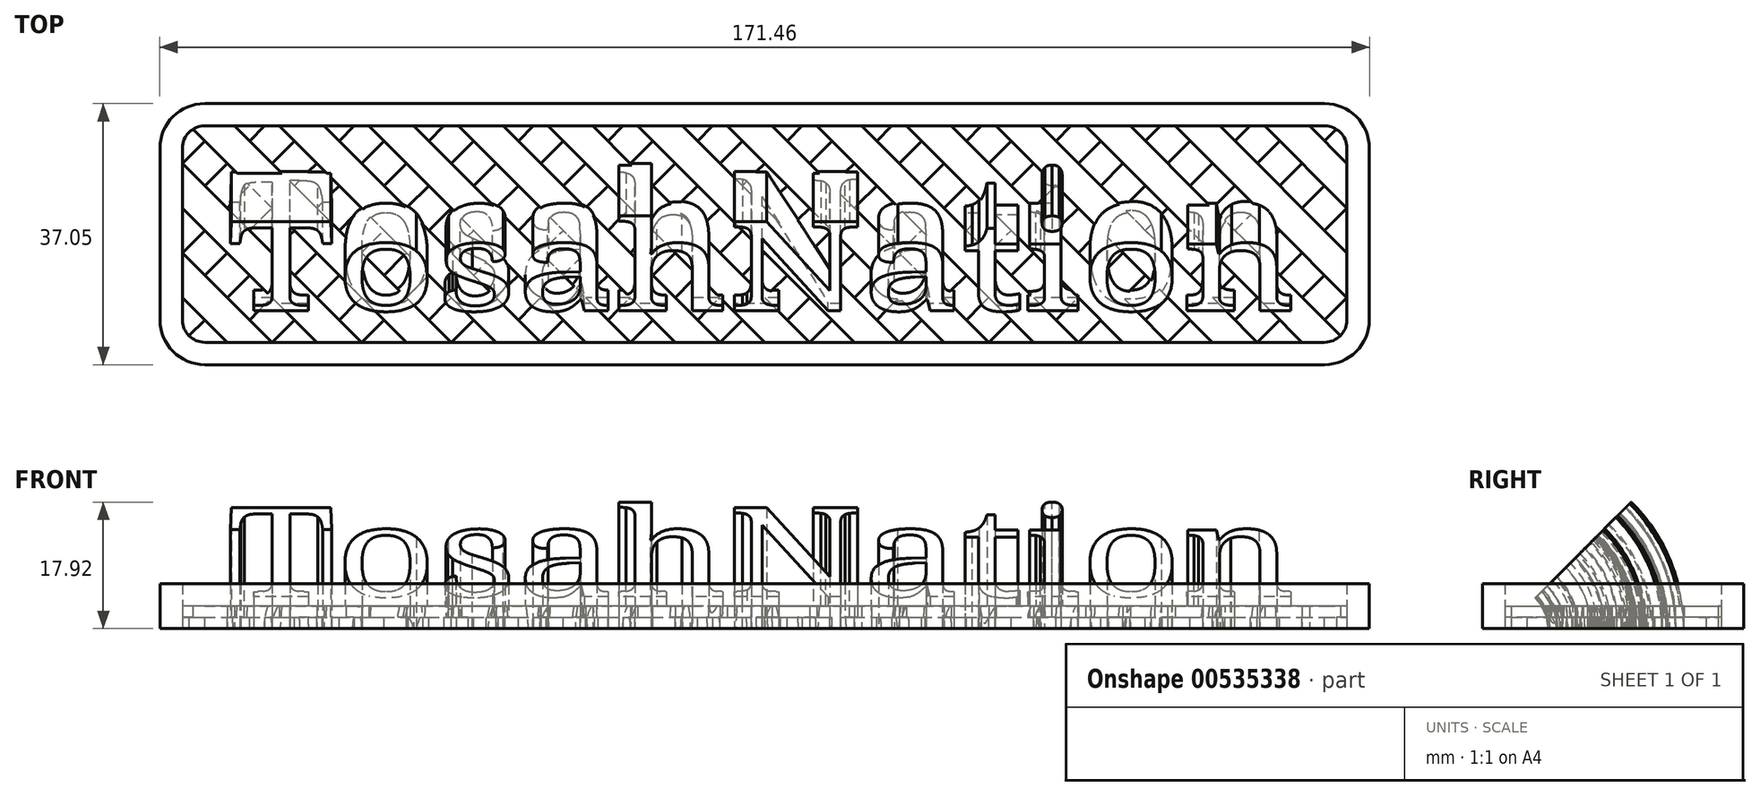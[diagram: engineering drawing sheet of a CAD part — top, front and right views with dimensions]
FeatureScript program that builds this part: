
annotation { "Feature Type Name" : "Feature", "Feature Type Description" : "" }
export const myFeature = defineFeature(function(context is Context, id is Id, definition is map)
    precondition{}
    {
        {
            var Q0;
            Q0=qCreatedBy(makeId("Top.planeOp"),FACE);
            var sketch = newSketch(context, id + "F0", { "sketchPlane" : qUnion([Q0])});
            skText(sketch, "E0", { "text": "TosahNation", "fontName": "NotoSerif-Regular.ttf"});
            skLineSegment(sketch, "E1", {"start": v(-76.2, 0) * mm, "end": v(-76.2, -6.35) * mm, "construction": true});
            skLineSegment(sketch, "E2", {"start": v(-76.2, -6.35) * mm, "end": v(-58.68, -6.35) * mm, "construction": true});
            const initialGuessF0  = {"E0": [-0.0762, 0, 1, 0, 0.018]};
            skSetInitialGuess(sketch, initialGuessF0);
            skSolve(sketch);
        }
        {
            var Q0;
            Q0=qCreatedBy(makeId("Top.planeOp"),FACE);
            var sketch = newSketch(context, id + "F1", { "sketchPlane" : qUnion([Q0])});
            skLineSegment(sketch, "E3", {"start": v(-82.55, -3.18) * mm, "end": v(-82.55, 21.17) * mm});
            skLineSegment(sketch, "E4", {"start": v(-79.37, 24.35) * mm, "end": v(79.37, 24.35) * mm});
            skLineSegment(sketch, "E5", {"start": v(82.55, 21.17) * mm, "end": v(82.55, -3.17) * mm});
            skLineSegment(sketch, "E6", {"start": v(79.37, -6.35) * mm, "end": v(-79.37, -6.35) * mm});
            skLineSegment(sketch, "E7", {"start": v(-81.62, -5.42) * mm, "end": v(-51.85, 24.35) * mm});
            skLineSegment(sketch, "E8.1.0.0", {"start": v(-76.2, -6.35) * mm, "end": v(-45.5, 24.35) * mm});
            skLineSegment(sketch, "E8.2.0.0", {"start": v(-69.85, -6.35) * mm, "end": v(-39.15, 24.35) * mm});
            skLineSegment(sketch, "E8.3.0.0", {"start": v(-63.5, -6.35) * mm, "end": v(-32.8, 24.35) * mm});
            skLineSegment(sketch, "E8.4.0.0", {"start": v(-57.15, -6.35) * mm, "end": v(-26.45, 24.35) * mm});
            skLineSegment(sketch, "E8.5.0.0", {"start": v(-50.8, -6.35) * mm, "end": v(-20.1, 24.35) * mm});
            skLineSegment(sketch, "E8.6.0.0", {"start": v(-44.45, -6.35) * mm, "end": v(-13.75, 24.35) * mm});
            skLineSegment(sketch, "E8.7.0.0", {"start": v(-38.1, -6.35) * mm, "end": v(-7.4, 24.35) * mm});
            skLineSegment(sketch, "E8.8.0.0", {"start": v(-31.75, -6.35) * mm, "end": v(-1.05, 24.35) * mm});
            skLineSegment(sketch, "E8.9.0.0", {"start": v(-25.4, -6.35) * mm, "end": v(5.3, 24.35) * mm});
            skLineSegment(sketch, "E8.10.0.0", {"start": v(-19.05, -6.35) * mm, "end": v(11.65, 24.35) * mm});
            skLineSegment(sketch, "E8.11.0.0", {"start": v(-12.7, -6.35) * mm, "end": v(18, 24.35) * mm});
            skLineSegment(sketch, "E8.12.0.0", {"start": v(-6.35, -6.35) * mm, "end": v(24.35, 24.35) * mm});
            skLineSegment(sketch, "E8.13.0.0", {"start": v(0, -6.35) * mm, "end": v(30.7, 24.35) * mm});
            skLineSegment(sketch, "E8.14.0.0", {"start": v(6.35, -6.35) * mm, "end": v(37.05, 24.35) * mm});
            skLineSegment(sketch, "E8.15.0.0", {"start": v(12.7, -6.35) * mm, "end": v(43.4, 24.35) * mm});
            skLineSegment(sketch, "E8.16.0.0", {"start": v(19.05, -6.35) * mm, "end": v(49.75, 24.35) * mm});
            skLineSegment(sketch, "E8.17.0.0", {"start": v(25.4, -6.35) * mm, "end": v(56.1, 24.35) * mm});
            skLineSegment(sketch, "E8.18.0.0", {"start": v(31.75, -6.35) * mm, "end": v(62.45, 24.35) * mm});
            skLineSegment(sketch, "E8.19.0.0", {"start": v(38.1, -6.35) * mm, "end": v(68.8, 24.35) * mm});
            skLineSegment(sketch, "E8.20.0.0", {"start": v(44.45, -6.35) * mm, "end": v(75.15, 24.35) * mm});
            skLineSegment(sketch, "E8.21.0.0", {"start": v(50.8, -6.35) * mm, "end": v(81.03, 23.88) * mm});
            skLineSegment(sketch, "E8.22.0.0", {"start": v(57.15, -6.35) * mm, "end": v(82.55, 19.05) * mm});
            skLineSegment(sketch, "E8.23.0.0", {"start": v(63.5, -6.35) * mm, "end": v(82.55, 12.7) * mm});
            skLineSegment(sketch, "E8.24.0.0", {"start": v(69.85, -6.35) * mm, "end": v(82.55, 6.35) * mm});
            skLineSegment(sketch, "E8.25.0.0", {"start": v(76.2, -6.35) * mm, "end": v(82.55, 0) * mm});
            skLineSegment(sketch, "E8.direction1", {"start": v(-82.55, -6.35) * mm, "end": v(-76.2, -6.35) * mm, "construction": true});
            skLineSegment(sketch, "E9.1.0.0", {"start": v(-82.55, 0) * mm, "end": v(-58.2, 24.35) * mm});
            skLineSegment(sketch, "E9.2.0.0", {"start": v(-82.55, 6.35) * mm, "end": v(-64.55, 24.35) * mm});
            skLineSegment(sketch, "E9.3.0.0", {"start": v(-82.55, 12.7) * mm, "end": v(-70.9, 24.35) * mm});
            skLineSegment(sketch, "E9.4.0.0", {"start": v(-82.55, 19.05) * mm, "end": v(-77.25, 24.35) * mm});
            skLineSegment(sketch, "E9.direction1", {"start": v(-82.55, -6.35) * mm, "end": v(-88.9, -6.35) * mm, "construction": true});
            skPoint(sketch, "E10.orphan", {"position": v(-107.95, -6.35) * mm});
            skPoint(sketch, "E11.orphan", {"position": v(-101.6, -6.35) * mm});
            skPoint(sketch, "E12.orphan", {"position": v(-95.25, -6.35) * mm});
            skPoint(sketch, "E13.orphan", {"position": v(-49.82, 51.78) * mm});
            skPoint(sketch, "E14.orphan", {"position": v(-43.47, 51.78) * mm});
            skPoint(sketch, "E15.orphan", {"position": v(-37.12, 51.78) * mm});
            skPoint(sketch, "E16.orphan", {"position": v(-30.77, 51.78) * mm});
            skPoint(sketch, "E17.orphan", {"position": v(-24.42, 51.78) * mm});
            skPoint(sketch, "E18.orphan", {"position": v(-18.07, 51.78) * mm});
            skPoint(sketch, "E19.orphan", {"position": v(-11.72, 51.78) * mm});
            skPoint(sketch, "E20.orphan", {"position": v(-5.37, 51.78) * mm});
            skPoint(sketch, "E21.orphan", {"position": v(0.98, 51.78) * mm});
            skPoint(sketch, "E22.orphan", {"position": v(7.33, 51.78) * mm});
            skPoint(sketch, "E23.orphan", {"position": v(13.68, 51.78) * mm});
            skPoint(sketch, "E24.orphan", {"position": v(20.03, 51.78) * mm});
            skPoint(sketch, "E25.orphan", {"position": v(58.13, 51.78) * mm});
            skPoint(sketch, "E26.orphan", {"position": v(64.48, 51.78) * mm});
            skPoint(sketch, "E27.orphan", {"position": v(70.83, 51.78) * mm});
            skPoint(sketch, "E28.orphan", {"position": v(77.18, 51.78) * mm});
            skPoint(sketch, "E29.orphan", {"position": v(83.53, 51.78) * mm});
            skPoint(sketch, "E30.orphan", {"position": v(89.88, 51.78) * mm});
            skPoint(sketch, "E31.orphan", {"position": v(96.23, 51.78) * mm});
            skPoint(sketch, "E32.orphan", {"position": v(102.58, 51.78) * mm});
            skPoint(sketch, "E33.orphan", {"position": v(108.93, 51.78) * mm});
            skPoint(sketch, "E34.orphan", {"position": v(115.28, 51.78) * mm});
            skPoint(sketch, "E35.orphan", {"position": v(121.63, 51.78) * mm});
            skPoint(sketch, "E36.orphan", {"position": v(127.98, 51.78) * mm});
            skPoint(sketch, "E37.orphan", {"position": v(134.33, 51.78) * mm});
            skPoint(sketch, "E38.visualSharp", {"position": v(-82.55, 24.35) * mm});
            skArc(sketch, "E38.filletArc", {"start": v(-79.37, 24.35) * mm, "mid": v(-81.62, 23.42) * mm, "end": v(-82.55, 21.17) * mm});
            skPoint(sketch, "E39.visualSharp", {"position": v(-82.55, -6.35) * mm});
            skArc(sketch, "E39.filletArc", {"start": v(-82.55, -3.18) * mm, "mid": v(-81.62, -5.42) * mm, "end": v(-79.37, -6.35) * mm});
            skPoint(sketch, "E40.visualSharp", {"position": v(82.55, 24.35) * mm});
            skArc(sketch, "E40.filletArc", {"start": v(82.55, 21.17) * mm, "mid": v(81.62, 23.42) * mm, "end": v(79.37, 24.35) * mm});
            skPoint(sketch, "E41.visualSharp", {"position": v(82.55, -6.35) * mm});
            skArc(sketch, "E41.filletArc", {"start": v(79.37, -6.35) * mm, "mid": v(81.62, -5.42) * mm, "end": v(82.55, -3.17) * mm});
            skArc(sketch, "E42.0", {"start": v(-85.72, -3.18) * mm, "mid": v(-83.87, -7.67) * mm, "end": v(-79.37, -9.53) * mm});
            skLineSegment(sketch, "E42.1", {"start": v(79.37, -9.52) * mm, "end": v(-79.37, -9.53) * mm});
            skLineSegment(sketch, "E42.2", {"start": v(-85.72, -3.18) * mm, "end": v(-85.72, 21.17) * mm});
            skArc(sketch, "E42.3", {"start": v(79.37, -9.53) * mm, "mid": v(83.87, -7.67) * mm, "end": v(85.72, -3.17) * mm});
            skArc(sketch, "E42.4", {"start": v(-79.37, 27.52) * mm, "mid": v(-83.87, 25.66) * mm, "end": v(-85.72, 21.17) * mm});
            skLineSegment(sketch, "E42.5", {"start": v(-79.37, 27.52) * mm, "end": v(79.37, 27.52) * mm});
            skArc(sketch, "E42.6", {"start": v(85.72, 21.17) * mm, "mid": v(83.87, 25.66) * mm, "end": v(79.37, 27.52) * mm});
            skLineSegment(sketch, "E42.7", {"start": v(85.72, 21.17) * mm, "end": v(85.72, -3.17) * mm});
            skSolve(sketch);
        }
        {
            var Q0;
            {var subQ54=sQuery(id+"F1.wireOp",EDGE,"E38.filletArc");Q0=makeQuery(id+"F1.imprint","IMPRINT",FACE,{"disambiguationData":[TD([[makeQuery(id+"F1.imprint","IMPRINT",EDGE,{"derivedFrom":subQ54}),-1.0]])]});}
            extrude(context, id + "F2", {"entities" : qUnion([Q0]), "depth" : 6.35 * mm, "offsetDistance" : 25.4 * mm});
        }
        {
            var Q0;
            {var subQ0=sQuery(id+"F1.wireOp",EDGE,"E8.15.0.0");Q0=makeQuery(id+"F1.imprint","IMPRINT",FACE,{"disambiguationData":[TD([[makeQuery(id+"F1.imprint","IMPRINT",EDGE,{"derivedFrom":subQ0}),-1.0]])]});}
            var Q1;
            {var subQ0=sQuery(id+"F1.wireOp",EDGE,"E8.17.0.0");Q1=makeQuery(id+"F1.imprint","IMPRINT",FACE,{"disambiguationData":[TD([[makeQuery(id+"F1.imprint","IMPRINT",EDGE,{"derivedFrom":subQ0}),-1.0]])]});}
            var Q2;
            {var subQ0=sQuery(id+"F1.wireOp",EDGE,"E8.19.0.0");Q2=makeQuery(id+"F1.imprint","IMPRINT",FACE,{"disambiguationData":[TD([[makeQuery(id+"F1.imprint","IMPRINT",EDGE,{"derivedFrom":subQ0}),-1.0]])]});}
            var Q3;
            {var subQ1=sQuery(id+"F1.wireOp",EDGE,"E8.21.0.0");Q3=makeQuery(id+"F1.imprint","IMPRINT",FACE,{"disambiguationData":[TD([[makeQuery(id+"F1.imprint","IMPRINT",EDGE,{"derivedFrom":subQ1}),-1.0]])]});}
            var Q4;
            {var subQ2=sQuery(id+"F1.wireOp",EDGE,"E8.25.0.0");Q4=makeQuery(id+"F1.imprint","IMPRINT",FACE,{"disambiguationData":[TD([[makeQuery(id+"F1.imprint","IMPRINT",EDGE,{"derivedFrom":subQ2}),-1.0]])]});}
            var Q5;
            {var subQ0=sQuery(id+"F1.wireOp",EDGE,"E8.23.0.0");Q5=makeQuery(id+"F1.imprint","IMPRINT",FACE,{"disambiguationData":[TD([[makeQuery(id+"F1.imprint","IMPRINT",EDGE,{"derivedFrom":subQ0}),-1.0]])]});}
            var Q6;
            {var subQ0=sQuery(id+"F1.wireOp",EDGE,"E8.13.0.0");Q6=makeQuery(id+"F1.imprint","IMPRINT",FACE,{"disambiguationData":[TD([[makeQuery(id+"F1.imprint","IMPRINT",EDGE,{"derivedFrom":subQ0}),-1.0]])]});}
            var Q7;
            {var subQ0=sQuery(id+"F1.wireOp",EDGE,"E8.11.0.0");Q7=makeQuery(id+"F1.imprint","IMPRINT",FACE,{"disambiguationData":[TD([[makeQuery(id+"F1.imprint","IMPRINT",EDGE,{"derivedFrom":subQ0}),-1.0]])]});}
            var Q8;
            {var subQ0=sQuery(id+"F1.wireOp",EDGE,"E8.9.0.0");Q8=makeQuery(id+"F1.imprint","IMPRINT",FACE,{"disambiguationData":[TD([[makeQuery(id+"F1.imprint","IMPRINT",EDGE,{"derivedFrom":subQ0}),-1.0]])]});}
            var Q9;
            {var subQ0=sQuery(id+"F1.wireOp",EDGE,"E8.7.0.0");Q9=makeQuery(id+"F1.imprint","IMPRINT",FACE,{"disambiguationData":[TD([[makeQuery(id+"F1.imprint","IMPRINT",EDGE,{"derivedFrom":subQ0}),-1.0]])]});}
            var Q10;
            {var subQ0=sQuery(id+"F1.wireOp",EDGE,"E8.5.0.0");Q10=makeQuery(id+"F1.imprint","IMPRINT",FACE,{"disambiguationData":[TD([[makeQuery(id+"F1.imprint","IMPRINT",EDGE,{"derivedFrom":subQ0}),-1.0]])]});}
            var Q11;
            {var subQ0=sQuery(id+"F1.wireOp",EDGE,"E8.3.0.0");Q11=makeQuery(id+"F1.imprint","IMPRINT",FACE,{"disambiguationData":[TD([[makeQuery(id+"F1.imprint","IMPRINT",EDGE,{"derivedFrom":subQ0}),-1.0]])]});}
            var Q12;
            {var subQ0=sQuery(id+"F1.wireOp",EDGE,"E8.1.0.0");Q12=makeQuery(id+"F1.imprint","IMPRINT",FACE,{"disambiguationData":[TD([[makeQuery(id+"F1.imprint","IMPRINT",EDGE,{"derivedFrom":subQ0}),-1.0]])]});}
            var Q13;
            {var subQ4=sQuery(id+"F1.wireOp",EDGE,"E7");Q13=makeQuery(id+"F1.imprint","IMPRINT",FACE,{"disambiguationData":[TD([[makeQuery(id+"F1.imprint","IMPRINT",EDGE,{"derivedFrom":subQ4}),1.0]])]});}
            var Q14;
            {var subQ0=sQuery(id+"F1.wireOp",EDGE,"E9.2.0.0");Q14=makeQuery(id+"F1.imprint","IMPRINT",FACE,{"disambiguationData":[TD([[makeQuery(id+"F1.imprint","IMPRINT",EDGE,{"derivedFrom":subQ0}),1.0]])]});}
            var Q15;
            {var subQ2=sQuery(id+"F1.wireOp",EDGE,"E9.4.0.0");Q15=makeQuery(id+"F1.imprint","IMPRINT",FACE,{"disambiguationData":[TD([[makeQuery(id+"F1.imprint","IMPRINT",EDGE,{"derivedFrom":subQ2}),1.0]])]});}
            extrude(context, id + "F3", {"entities" : qUnion([Q0, Q1, Q2, Q3, Q4, Q5, Q6, Q7, Q8, Q9, Q10, Q11, Q12, Q13, Q14, Q15]), "operationType" : NewBodyOperationType.ADD, "depth" : 1.59 * mm, "offsetDistance" : 25.4 * mm});
        }
        {
            var Q0;
            Q0=qCreatedBy(makeId("Top.planeOp"),FACE);
            var sketch = newSketch(context, id + "F4", { "sketchPlane" : qUnion([Q0])});
            skLineSegment(sketch, "E43", {"start": v(82.55, -6.35) * mm, "end": v(51.85, 24.35) * mm});
            skLineSegment(sketch, "E44.1.0.0", {"start": v(76.2, -6.35) * mm, "end": v(45.5, 24.35) * mm});
            skLineSegment(sketch, "E44.2.0.0", {"start": v(69.85, -6.35) * mm, "end": v(39.15, 24.35) * mm});
            skLineSegment(sketch, "E44.3.0.0", {"start": v(63.5, -6.35) * mm, "end": v(32.8, 24.35) * mm});
            skLineSegment(sketch, "E44.4.0.0", {"start": v(57.15, -6.35) * mm, "end": v(26.45, 24.35) * mm});
            skLineSegment(sketch, "E44.5.0.0", {"start": v(50.8, -6.35) * mm, "end": v(20.1, 24.35) * mm});
            skLineSegment(sketch, "E44.6.0.0", {"start": v(44.45, -6.35) * mm, "end": v(13.75, 24.35) * mm});
            skLineSegment(sketch, "E44.7.0.0", {"start": v(38.1, -6.35) * mm, "end": v(7.4, 24.35) * mm});
            skLineSegment(sketch, "E44.8.0.0", {"start": v(31.75, -6.35) * mm, "end": v(1.05, 24.35) * mm});
            skLineSegment(sketch, "E44.9.0.0", {"start": v(25.4, -6.35) * mm, "end": v(-5.3, 24.35) * mm});
            skLineSegment(sketch, "E44.10.0.0", {"start": v(19.05, -6.35) * mm, "end": v(-11.65, 24.35) * mm});
            skLineSegment(sketch, "E44.11.0.0", {"start": v(12.7, -6.35) * mm, "end": v(-18, 24.35) * mm});
            skLineSegment(sketch, "E44.12.0.0", {"start": v(6.35, -6.35) * mm, "end": v(-24.35, 24.35) * mm});
            skLineSegment(sketch, "E44.13.0.0", {"start": v(0, -6.35) * mm, "end": v(-30.7, 24.35) * mm});
            skLineSegment(sketch, "E44.14.0.0", {"start": v(-6.35, -6.35) * mm, "end": v(-37.05, 24.35) * mm});
            skLineSegment(sketch, "E44.15.0.0", {"start": v(-12.7, -6.35) * mm, "end": v(-43.4, 24.35) * mm});
            skLineSegment(sketch, "E44.16.0.0", {"start": v(-19.05, -6.35) * mm, "end": v(-49.75, 24.35) * mm});
            skLineSegment(sketch, "E44.17.0.0", {"start": v(-25.4, -6.35) * mm, "end": v(-56.1, 24.35) * mm});
            skLineSegment(sketch, "E44.18.0.0", {"start": v(-31.75, -6.35) * mm, "end": v(-62.45, 24.35) * mm});
            skLineSegment(sketch, "E44.19.0.0", {"start": v(-38.1, -6.35) * mm, "end": v(-68.8, 24.35) * mm});
            skLineSegment(sketch, "E44.20.0.0", {"start": v(-44.45, -6.35) * mm, "end": v(-75.15, 24.35) * mm});
            skLineSegment(sketch, "E44.21.0.0", {"start": v(-50.8, -6.35) * mm, "end": v(-81.5, 24.35) * mm});
            skLineSegment(sketch, "E44.22.0.0", {"start": v(-57.15, -6.35) * mm, "end": v(-82.55, 19.05) * mm});
            skLineSegment(sketch, "E44.23.0.0", {"start": v(-63.5, -6.35) * mm, "end": v(-82.55, 12.7) * mm});
            skLineSegment(sketch, "E44.24.0.0", {"start": v(-69.85, -6.35) * mm, "end": v(-82.55, 6.35) * mm});
            skLineSegment(sketch, "E44.25.0.0", {"start": v(-76.2, -6.35) * mm, "end": v(-82.55, 0) * mm});
            skLineSegment(sketch, "E44.direction1", {"start": v(82.55, -6.35) * mm, "end": v(76.2, -6.35) * mm, "construction": true});
            skLineSegment(sketch, "E45.bottom", {"start": v(-82.55, 24.35) * mm, "end": v(82.55, 24.35) * mm});
            skLineSegment(sketch, "E45.top", {"start": v(-82.55, -6.35) * mm, "end": v(82.55, -6.35) * mm});
            skLineSegment(sketch, "E45.left", {"start": v(-82.55, 24.35) * mm, "end": v(-82.55, -6.35) * mm});
            skLineSegment(sketch, "E45.right", {"start": v(82.55, 24.35) * mm, "end": v(82.55, -6.35) * mm});
            skLineSegment(sketch, "E46.1.0.0", {"start": v(82.55, 0) * mm, "end": v(58.2, 24.35) * mm});
            skLineSegment(sketch, "E46.2.0.0", {"start": v(82.55, 6.35) * mm, "end": v(64.55, 24.35) * mm});
            skLineSegment(sketch, "E46.3.0.0", {"start": v(82.55, 12.7) * mm, "end": v(70.9, 24.35) * mm});
            skLineSegment(sketch, "E46.4.0.0", {"start": v(82.55, 19.05) * mm, "end": v(77.25, 24.35) * mm});
            skLineSegment(sketch, "E46.direction1", {"start": v(82.55, -6.35) * mm, "end": v(88.9, -6.35) * mm, "construction": true});
            skPoint(sketch, "E47.orphan", {"position": v(107.95, -6.35) * mm});
            skPoint(sketch, "E48.orphan", {"position": v(101.6, -6.35) * mm});
            skPoint(sketch, "E49.orphan", {"position": v(95.25, -6.35) * mm});
            skPoint(sketch, "E50.orphan", {"position": v(67.41, 34.19) * mm});
            skPoint(sketch, "E51.orphan", {"position": v(61.06, 34.19) * mm});
            skPoint(sketch, "E52.orphan", {"position": v(54.71, 34.19) * mm});
            skPoint(sketch, "E53.orphan", {"position": v(48.36, 34.19) * mm});
            skPoint(sketch, "E54.orphan", {"position": v(42.01, 34.19) * mm});
            skPoint(sketch, "E55.orphan", {"position": v(35.66, 34.19) * mm});
            skPoint(sketch, "E56.orphan", {"position": v(29.31, 34.19) * mm});
            skPoint(sketch, "E57.orphan", {"position": v(22.96, 34.19) * mm});
            skPoint(sketch, "E58.orphan", {"position": v(16.61, 34.19) * mm});
            skPoint(sketch, "E59.orphan", {"position": v(10.26, 34.19) * mm});
            skPoint(sketch, "E60.orphan", {"position": v(3.91, 34.19) * mm});
            skPoint(sketch, "E61.orphan", {"position": v(-2.44, 34.19) * mm});
            skPoint(sketch, "E62.orphan", {"position": v(-8.79, 34.19) * mm});
            skPoint(sketch, "E63.orphan", {"position": v(-15.14, 34.19) * mm});
            skPoint(sketch, "E64.orphan", {"position": v(-21.49, 34.19) * mm});
            skPoint(sketch, "E65.orphan", {"position": v(-27.84, 34.19) * mm});
            skPoint(sketch, "E66.orphan", {"position": v(-34.19, 34.19) * mm});
            skPoint(sketch, "E67.orphan", {"position": v(-40.54, 34.19) * mm});
            skPoint(sketch, "E68.orphan", {"position": v(-46.89, 34.19) * mm});
            skPoint(sketch, "E69.orphan", {"position": v(-53.24, 34.19) * mm});
            skPoint(sketch, "E70.orphan", {"position": v(-59.59, 34.19) * mm});
            skPoint(sketch, "E71.orphan", {"position": v(-65.94, 34.19) * mm});
            skPoint(sketch, "E72.orphan", {"position": v(-72.29, 34.19) * mm});
            skPoint(sketch, "E73.orphan", {"position": v(-78.64, 34.19) * mm});
            skPoint(sketch, "E74.orphan", {"position": v(-84.99, 34.19) * mm});
            skPoint(sketch, "E75.orphan", {"position": v(-91.34, 34.19) * mm});
            skPoint(sketch, "E76.orphan", {"position": v(-97.69, 34.19) * mm});
            skPoint(sketch, "E77.orphan", {"position": v(-104.04, 34.19) * mm});
            skPoint(sketch, "E78.orphan", {"position": v(-110.39, 34.19) * mm});
            skPoint(sketch, "E79.orphan", {"position": v(-116.74, 34.19) * mm});
            skSolve(sketch);
        }
        {
            var Q0;
            {var subQ0=sQuery(id+"F4.wireOp",EDGE,"E44.24.0.0");Q0=makeQuery(id+"F4.imprint","IMPRINT",FACE,{"disambiguationData":[TD([[makeQuery(id+"F4.imprint","IMPRINT",EDGE,{"derivedFrom":subQ0}),1.0]])]});}
            var Q1;
            {var subQ0=sQuery(id+"F4.wireOp",EDGE,"E44.22.0.0");Q1=makeQuery(id+"F4.imprint","IMPRINT",FACE,{"disambiguationData":[TD([[makeQuery(id+"F4.imprint","IMPRINT",EDGE,{"derivedFrom":subQ0}),1.0]])]});}
            var Q2;
            {var subQ0=sQuery(id+"F4.wireOp",EDGE,"E44.20.0.0");Q2=makeQuery(id+"F4.imprint","IMPRINT",FACE,{"disambiguationData":[TD([[makeQuery(id+"F4.imprint","IMPRINT",EDGE,{"derivedFrom":subQ0}),1.0]])]});}
            var Q3;
            {var subQ0=sQuery(id+"F4.wireOp",EDGE,"E44.18.0.0");Q3=makeQuery(id+"F4.imprint","IMPRINT",FACE,{"disambiguationData":[TD([[makeQuery(id+"F4.imprint","IMPRINT",EDGE,{"derivedFrom":subQ0}),1.0]])]});}
            var Q4;
            {var subQ0=sQuery(id+"F4.wireOp",EDGE,"E44.16.0.0");Q4=makeQuery(id+"F4.imprint","IMPRINT",FACE,{"disambiguationData":[TD([[makeQuery(id+"F4.imprint","IMPRINT",EDGE,{"derivedFrom":subQ0}),1.0]])]});}
            var Q5;
            {var subQ0=sQuery(id+"F4.wireOp",EDGE,"E44.14.0.0");Q5=makeQuery(id+"F4.imprint","IMPRINT",FACE,{"disambiguationData":[TD([[makeQuery(id+"F4.imprint","IMPRINT",EDGE,{"derivedFrom":subQ0}),1.0]])]});}
            var Q6;
            {var subQ0=sQuery(id+"F4.wireOp",EDGE,"E44.12.0.0");Q6=makeQuery(id+"F4.imprint","IMPRINT",FACE,{"disambiguationData":[TD([[makeQuery(id+"F4.imprint","IMPRINT",EDGE,{"derivedFrom":subQ0}),1.0]])]});}
            extrude(context, id + "F5", {"entities" : qUnion([Q0, Q1, Q2, Q3, Q4, Q5, Q6]), "operationType" : NewBodyOperationType.ADD, "depth" : 3.17 * mm, "offsetDistance" : 25.4 * mm});
        }
        {
            var Q0;
            {var subQ0=sQuery(id+"F4.wireOp",EDGE,"E44.10.0.0");Q0=makeQuery(id+"F4.imprint","IMPRINT",FACE,{"disambiguationData":[TD([[makeQuery(id+"F4.imprint","IMPRINT",EDGE,{"derivedFrom":subQ0}),1.0]])]});}
            var Q1;
            {var subQ0=sQuery(id+"F4.wireOp",EDGE,"E44.8.0.0");Q1=makeQuery(id+"F4.imprint","IMPRINT",FACE,{"disambiguationData":[TD([[makeQuery(id+"F4.imprint","IMPRINT",EDGE,{"derivedFrom":subQ0}),1.0]])]});}
            var Q2;
            {var subQ0=sQuery(id+"F4.wireOp",EDGE,"E44.6.0.0");Q2=makeQuery(id+"F4.imprint","IMPRINT",FACE,{"disambiguationData":[TD([[makeQuery(id+"F4.imprint","IMPRINT",EDGE,{"derivedFrom":subQ0}),1.0]])]});}
            var Q3;
            {var subQ0=sQuery(id+"F4.wireOp",EDGE,"E44.4.0.0");Q3=makeQuery(id+"F4.imprint","IMPRINT",FACE,{"disambiguationData":[TD([[makeQuery(id+"F4.imprint","IMPRINT",EDGE,{"derivedFrom":subQ0}),1.0]])]});}
            var Q4;
            {var subQ0=sQuery(id+"F4.wireOp",EDGE,"E44.2.0.0");Q4=makeQuery(id+"F4.imprint","IMPRINT",FACE,{"disambiguationData":[TD([[makeQuery(id+"F4.imprint","IMPRINT",EDGE,{"derivedFrom":subQ0}),1.0]])]});}
            var Q5;
            {var subQ0=sQuery(id+"F4.wireOp",EDGE,"E43");Q5=makeQuery(id+"F4.imprint","IMPRINT",FACE,{"disambiguationData":[TD([[makeQuery(id+"F4.imprint","IMPRINT",EDGE,{"derivedFrom":subQ0}),1.0]])]});}
            var Q6;
            {var subQ0=sQuery(id+"F4.wireOp",EDGE,"E46.1.0.0");Q6=makeQuery(id+"F4.imprint","IMPRINT",FACE,{"disambiguationData":[TD([[makeQuery(id+"F4.imprint","IMPRINT",EDGE,{"derivedFrom":subQ0}),-1.0]])]});}
            var Q7;
            {var subQ0=sQuery(id+"F4.wireOp",EDGE,"E46.3.0.0");Q7=makeQuery(id+"F4.imprint","IMPRINT",FACE,{"disambiguationData":[TD([[makeQuery(id+"F4.imprint","IMPRINT",EDGE,{"derivedFrom":subQ0}),-1.0]])]});}
            extrude(context, id + "F6", {"entities" : qUnion([Q0, Q1, Q2, Q3, Q4, Q5, Q6, Q7]), "operationType" : NewBodyOperationType.ADD, "depth" : 3.17 * mm, "offsetDistance" : 25.4 * mm});
        }
        {
            var Q0;
            Q0 = qSketchRegion(id + "F0", true);
            var Q1;
            Q1=sQuery(id+"F0.wireOp",EDGE,"E2");
            revolve(context, id + "F7", {"operationType" : NewBodyOperationType.ADD, "entities" : qUnion([Q0]), "axis" : qUnion([Q1]), "revolveType" : RevolveType.ONE_DIRECTION, "angle" : 45 * degree});
        }
    });
